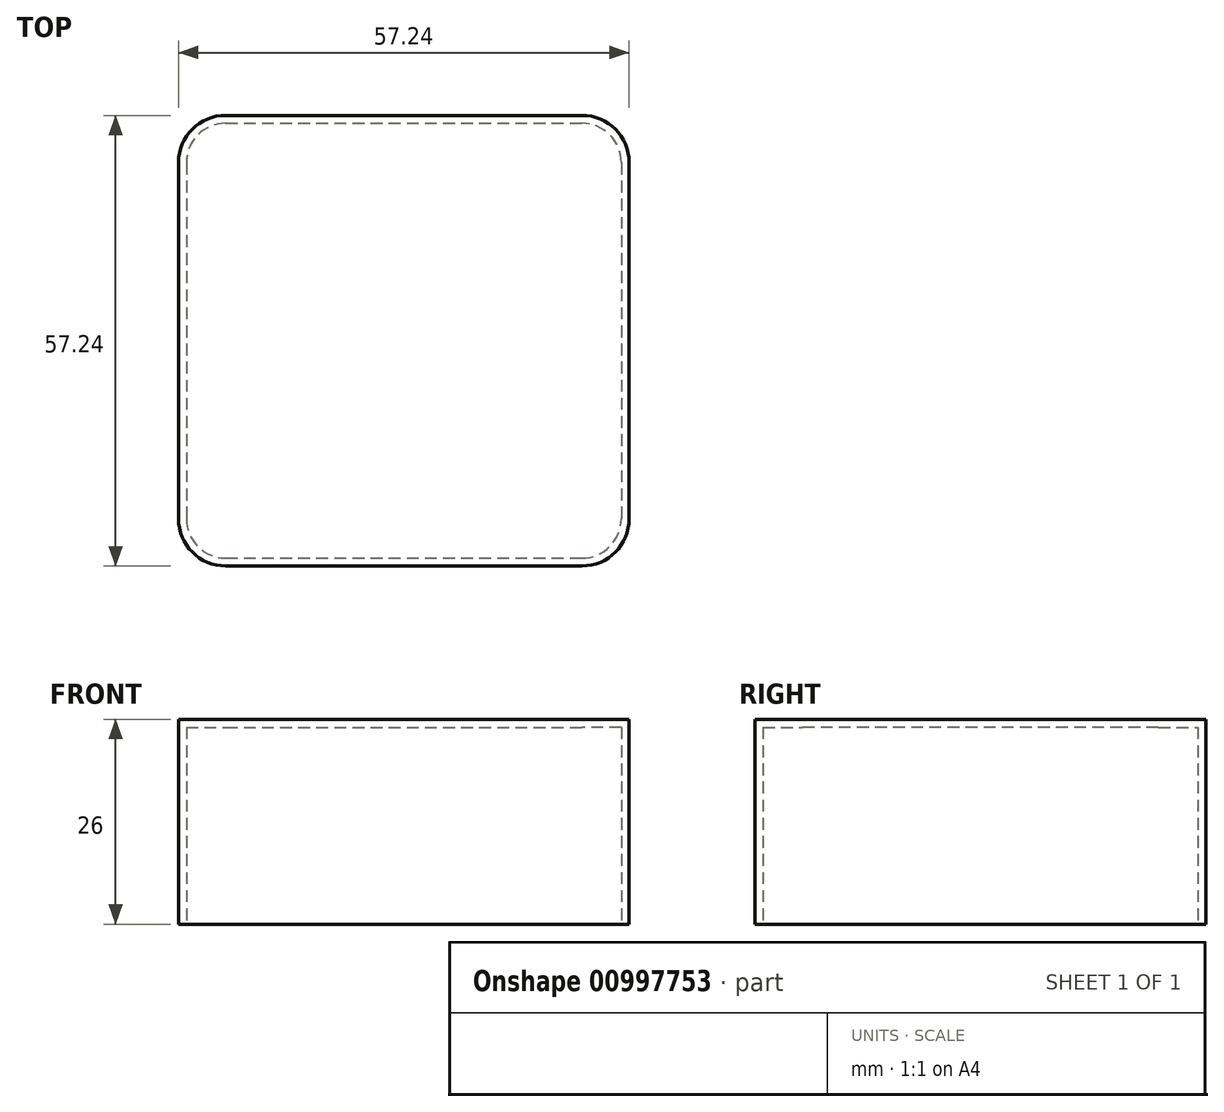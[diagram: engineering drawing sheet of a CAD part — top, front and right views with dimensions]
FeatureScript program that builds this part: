
annotation { "Feature Type Name" : "Feature", "Feature Type Description" : "" }
export const myFeature = defineFeature(function(context is Context, id is Id, definition is map)
    precondition{}
    {
        {
            var Q0;
            Q0=qCreatedBy(makeId("Top.planeOp"),FACE);
            var sketch = newSketch(context, id + "F0", { "sketchPlane" : qUnion([Q0])});
            skLineSegment(sketch, "E0.bottom", {"start": v(-22.62, 27.62) * mm, "end": v(22.62, 27.62) * mm});
            skLineSegment(sketch, "E0.top", {"start": v(-22.62, -27.62) * mm, "end": v(22.62, -27.62) * mm});
            skLineSegment(sketch, "E0.left", {"start": v(-27.62, 22.62) * mm, "end": v(-27.62, -22.62) * mm});
            skLineSegment(sketch, "E0.right", {"start": v(27.62, 22.62) * mm, "end": v(27.62, -22.62) * mm});
            skPoint(sketch, "E0.middle", {"position": v(0, 0) * mm});
            skPoint(sketch, "E1.visualSharp", {"position": v(-27.62, 27.62) * mm});
            skArc(sketch, "E1.filletArc", {"start": v(-22.62, 27.62) * mm, "mid": v(-26.16, 26.16) * mm, "end": v(-27.62, 22.62) * mm});
            skPoint(sketch, "E2.visualSharp", {"position": v(27.62, 27.62) * mm});
            skArc(sketch, "E2.filletArc", {"start": v(27.62, 22.62) * mm, "mid": v(26.16, 26.16) * mm, "end": v(22.62, 27.62) * mm});
            skPoint(sketch, "E3.visualSharp", {"position": v(27.62, -27.62) * mm});
            skArc(sketch, "E3.filletArc", {"start": v(22.62, -27.62) * mm, "mid": v(26.16, -26.16) * mm, "end": v(27.62, -22.62) * mm});
            skPoint(sketch, "E4.visualSharp", {"position": v(-27.62, -27.62) * mm});
            skArc(sketch, "E4.filletArc", {"start": v(-27.62, -22.62) * mm, "mid": v(-26.16, -26.16) * mm, "end": v(-22.62, -27.62) * mm});
            skArc(sketch, "E5.0", {"start": v(-22.62, 28.62) * mm, "mid": v(-26.86, 26.86) * mm, "end": v(-28.62, 22.62) * mm});
            skLineSegment(sketch, "E5.1", {"start": v(-28.62, 22.62) * mm, "end": v(-28.62, -22.62) * mm});
            skLineSegment(sketch, "E5.2", {"start": v(-22.62, 28.62) * mm, "end": v(22.62, 28.62) * mm});
            skArc(sketch, "E5.3", {"start": v(-28.62, -22.62) * mm, "mid": v(-26.86, -26.86) * mm, "end": v(-22.62, -28.62) * mm});
            skArc(sketch, "E5.4", {"start": v(28.62, 22.62) * mm, "mid": v(26.86, 26.86) * mm, "end": v(22.62, 28.62) * mm});
            skLineSegment(sketch, "E5.5", {"start": v(28.62, 22.62) * mm, "end": v(28.62, -22.62) * mm});
            skArc(sketch, "E5.6", {"start": v(22.62, -28.62) * mm, "mid": v(26.86, -26.86) * mm, "end": v(28.62, -22.62) * mm});
            skLineSegment(sketch, "E5.7", {"start": v(-22.62, -28.62) * mm, "end": v(22.62, -28.62) * mm});
            skSolve(sketch);
        }
        {
            var Q0;
            Q0 = qSketchRegion(id + "F0", true);
            extrude(context, id + "F1", {"entities" : qUnion([Q0]), "depth" : 25 * mm, "offsetDistance" : 25 * mm});
        }
        {
            var Q0;
            Q0=makeQuery(id+"F1.opExtrude","CAP_FACE",FACE,{"disambiguationData":[OSD([sQuery(id+"F0.wireOp",EDGE,"E0.bottom"),sQuery(id+"F0.wireOp",EDGE,"E0.top"),sQuery(id+"F0.wireOp",EDGE,"E0.left"),sQuery(id+"F0.wireOp",EDGE,"E0.right"),sQuery(id+"F0.wireOp",EDGE,"E1.filletArc"),sQuery(id+"F0.wireOp",EDGE,"E2.filletArc"),sQuery(id+"F0.wireOp",EDGE,"E3.filletArc"),sQuery(id+"F0.wireOp",EDGE,"E4.filletArc"),sQuery(id+"F0.wireOp",EDGE,"E5.0"),sQuery(id+"F0.wireOp",EDGE,"E5.1"),sQuery(id+"F0.wireOp",EDGE,"E5.2"),sQuery(id+"F0.wireOp",EDGE,"E5.3"),sQuery(id+"F0.wireOp",EDGE,"E5.4"),sQuery(id+"F0.wireOp",EDGE,"E5.5"),sQuery(id+"F0.wireOp",EDGE,"E5.6"),sQuery(id+"F0.wireOp",EDGE,"E5.7")])],"isStart":false});
            var sketch = newSketch(context, id + "F2", { "sketchPlane" : qUnion([Q0])});
            skLineSegment(sketch, "E6.bottom", {"start": v(-46.8, 40.87) * mm, "end": v(46.8, 40.87) * mm});
            skLineSegment(sketch, "E6.top", {"start": v(-46.8, -40.87) * mm, "end": v(46.8, -40.87) * mm});
            skLineSegment(sketch, "E6.left", {"start": v(-46.8, 40.87) * mm, "end": v(-46.8, -40.87) * mm});
            skLineSegment(sketch, "E6.right", {"start": v(46.8, 40.87) * mm, "end": v(46.8, -40.87) * mm});
            skPoint(sketch, "E6.middle", {"position": v(0, 0) * mm});
            skSolve(sketch);
        }
        {
            var Q0;
            Q0=makeQuery(id+"F2.imprint","IMPRINT",FACE,{"disambiguationData":[TD([[makeQuery(id+"F2.imprint","IMPRINT",EDGE,{"derivedFrom":makeQuery(id+"F1.opExtrude","CAP_EDGE",EDGE,{"disambiguationData":[OSD([sQuery(id+"F0.wireOp",EDGE,"E0.bottom")])],"isStart":false})}),-1.0]])]});
            var Q1;
            Q1=makeQuery(id+"F2.imprint","IMPRINT",FACE,{"disambiguationData":[TD([[makeQuery(id+"F2.imprint","IMPRINT",EDGE,{"derivedFrom":makeQuery(id+"F1.opExtrude","CAP_EDGE",EDGE,{"disambiguationData":[OSD([sQuery(id+"F0.wireOp",EDGE,"E0.bottom")])],"isStart":false})}),1.0]])]});
            extrude(context, id + "F3", {"entities" : qUnion([Q0, Q1]), "operationType" : NewBodyOperationType.ADD, "depth" : 1 * mm, "offsetDistance" : 25 * mm});
        }
    });
